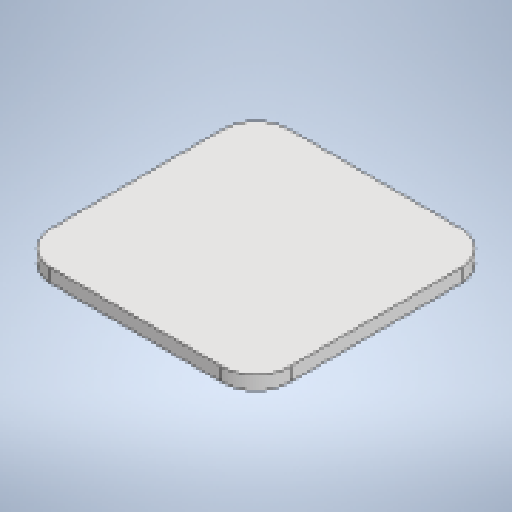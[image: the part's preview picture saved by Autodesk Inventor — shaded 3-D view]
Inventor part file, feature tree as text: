
AUTODESK INVENTOR PART (.ipt)
format: ipt  version: 2025.1 (Build 291241020, 241B)  size: 163,840 bytes
history: native  units: mm
features: other x2, sheet_metal_op x1, chamfer x1, sketch x1
ambient origin geometry x8: Origin, YZ Plane, XZ Plane, XY Plane, X Axis, Y Axis, Z Axis, Center Point
bodies: Solid1 (feature_tree)
feature tree (5):
  sheet_metal_op  "Face1"
  chamfer  "Corner Round1"
  sketch  "Sketch1"  dims[d0=140.0mm d1=140.0mm d2=8.0mm d22=20.0mm]
  other  "Plate1"
  other  "Definition1"
